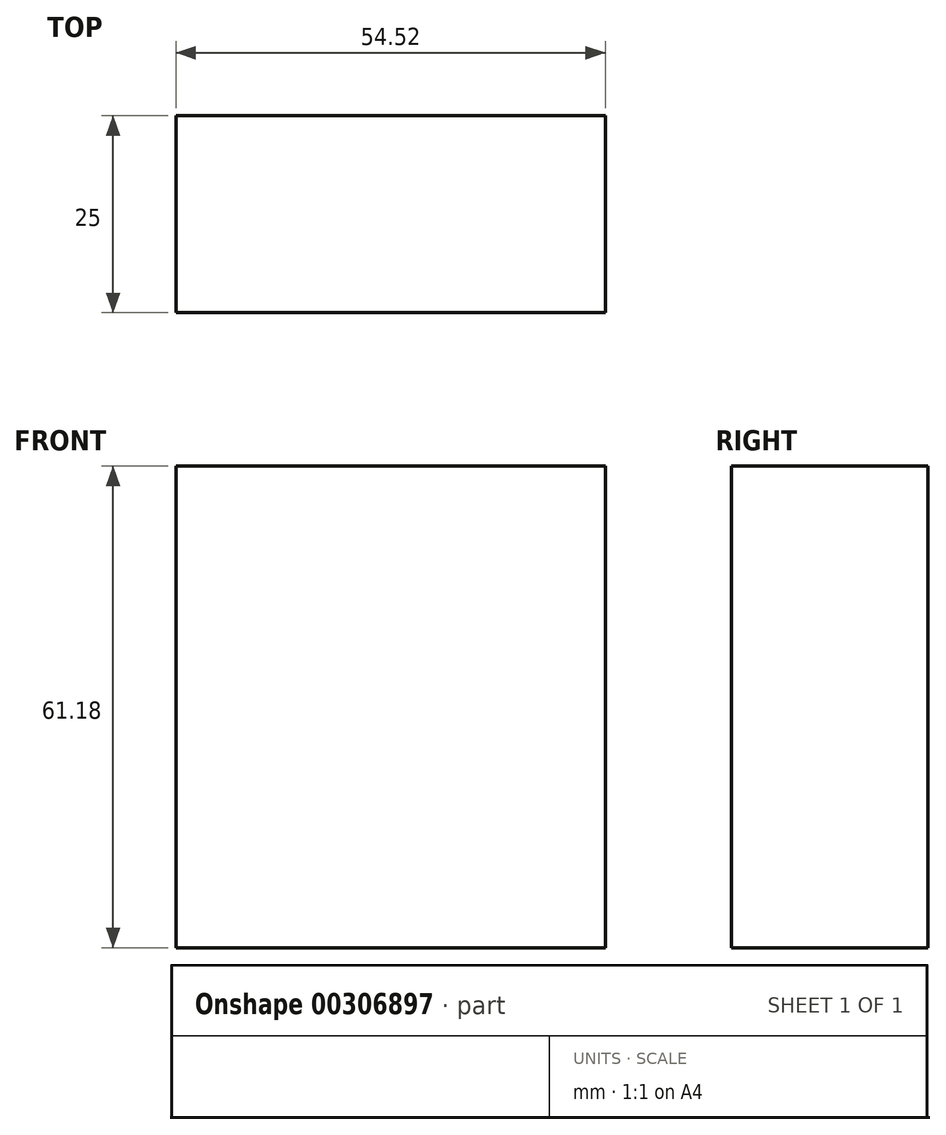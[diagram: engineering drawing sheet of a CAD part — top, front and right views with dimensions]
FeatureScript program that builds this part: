
annotation { "Feature Type Name" : "Feature", "Feature Type Description" : "" }
export const myFeature = defineFeature(function(context is Context, id is Id, definition is map)
    precondition{}
    {
        {
            var Q0;
            Q0=qCreatedBy(makeId("Front.planeOp"),FACE);
            var sketch = newSketch(context, id + "F0", { "sketchPlane" : qUnion([Q0])});
            skLineSegment(sketch, "E0.bottom", {"start": v(-85.68, 18.43) * mm, "end": v(-31.16, 18.43) * mm});
            skLineSegment(sketch, "E0.top", {"start": v(-85.68, 79.6) * mm, "end": v(-31.16, 79.6) * mm});
            skLineSegment(sketch, "E0.left", {"start": v(-85.68, 18.43) * mm, "end": v(-85.68, 79.6) * mm});
            skLineSegment(sketch, "E0.right", {"start": v(-31.16, 18.43) * mm, "end": v(-31.16, 79.6) * mm});
            skPoint(sketch, "E0.middle", {"position": v(-58.42, 49.02) * mm});
            skSolve(sketch);
        }
        {
            var Q0;
            Q0=makeQuery(id+"F0.imprint","IMPRINT",FACE,{"disambiguationData":[TD([[makeQuery(id+"F0.imprint","IMPRINT",EDGE,{"derivedFrom":sQuery(id+"F0.wireOp",EDGE,"E0.bottom")}),1.0]])]});
            extrude(context, id + "F1", {"entities" : qUnion([Q0]), "depth" : 25 * mm});
        }
    });
